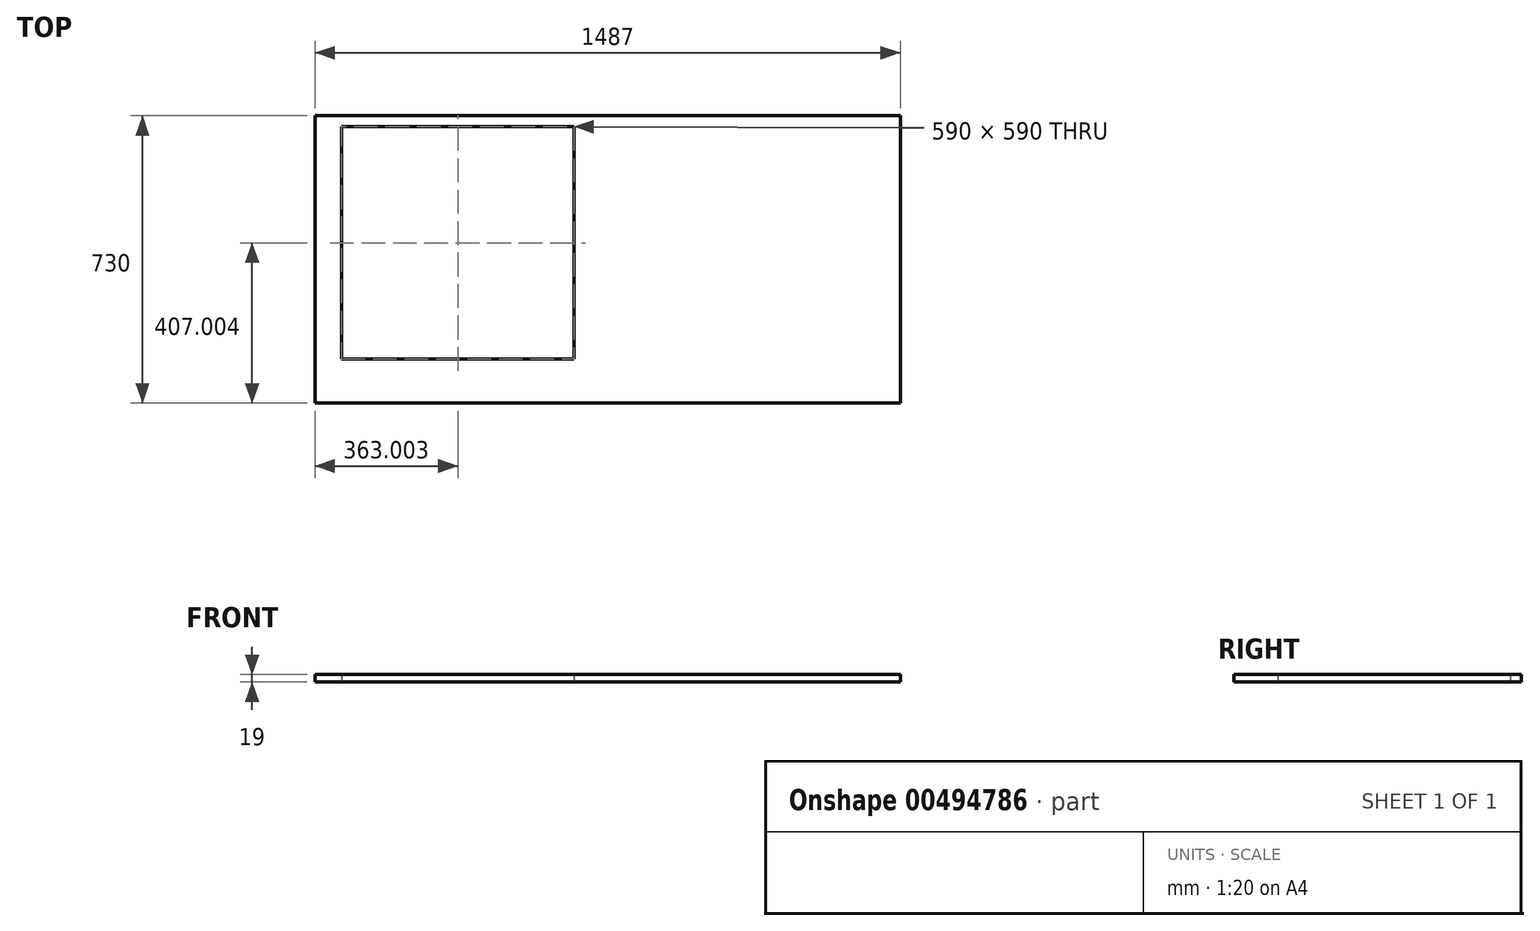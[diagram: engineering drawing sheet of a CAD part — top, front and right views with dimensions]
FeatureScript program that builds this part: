
annotation { "Feature Type Name" : "Feature", "Feature Type Description" : "" }
export const myFeature = defineFeature(function(context is Context, id is Id, definition is map)
    precondition{}
    {
        {
            var Q0;
            Q0=qCreatedBy(makeId("Top.planeOp"),FACE);
            var sketch = newSketch(context, id + "F0", { "sketchPlane" : qUnion([Q0])});
            skLineSegment(sketch, "E0.bottom", {"start": v(-63.4, -41.76) * mm, "end": v(1423.6, -41.76) * mm});
            skLineSegment(sketch, "E0.top", {"start": v(-63.4, 688.24) * mm, "end": v(1423.6, 688.24) * mm});
            skLineSegment(sketch, "E0.left", {"start": v(-63.4, -41.76) * mm, "end": v(-63.4, 688.24) * mm});
            skLineSegment(sketch, "E0.right", {"start": v(1423.6, -41.76) * mm, "end": v(1423.6, 688.24) * mm});
            skSolve(sketch);
        }
        {
            var Q0;
            Q0=makeQuery(id+"F0.imprint","IMPRINT",FACE,{"disambiguationData":[TD([[makeQuery(id+"F0.imprint","IMPRINT",EDGE,{"derivedFrom":sQuery(id+"F0.wireOp",EDGE,"E0.bottom")}),1.0]])]});
            extrude(context, id + "F1", {"entities" : qUnion([Q0]), "depth" : 19 * mm});
        }
        {
            var Q0;
            Q0=qCreatedBy(makeId("Top.planeOp"),FACE);
            var sketch = newSketch(context, id + "F2", { "sketchPlane" : qUnion([Q0])});
            skLineSegment(sketch, "E1.bottom", {"start": v(4.6, 70.24) * mm, "end": v(594.6, 70.24) * mm});
            skLineSegment(sketch, "E1.top", {"start": v(4.6, 660.24) * mm, "end": v(594.6, 660.24) * mm});
            skLineSegment(sketch, "E1.left", {"start": v(4.6, 70.24) * mm, "end": v(4.6, 660.24) * mm});
            skLineSegment(sketch, "E1.right", {"start": v(594.6, 70.24) * mm, "end": v(594.6, 660.24) * mm});
            skSolve(sketch);
        }
        {
            var Q0;
            Q0 = qSketchRegion(id + "F2", true);
            extrude(context, id + "F3", {"entities" : qUnion([Q0]), "operationType" : NewBodyOperationType.REMOVE, "depth" : 25 * mm});
        }
    });
